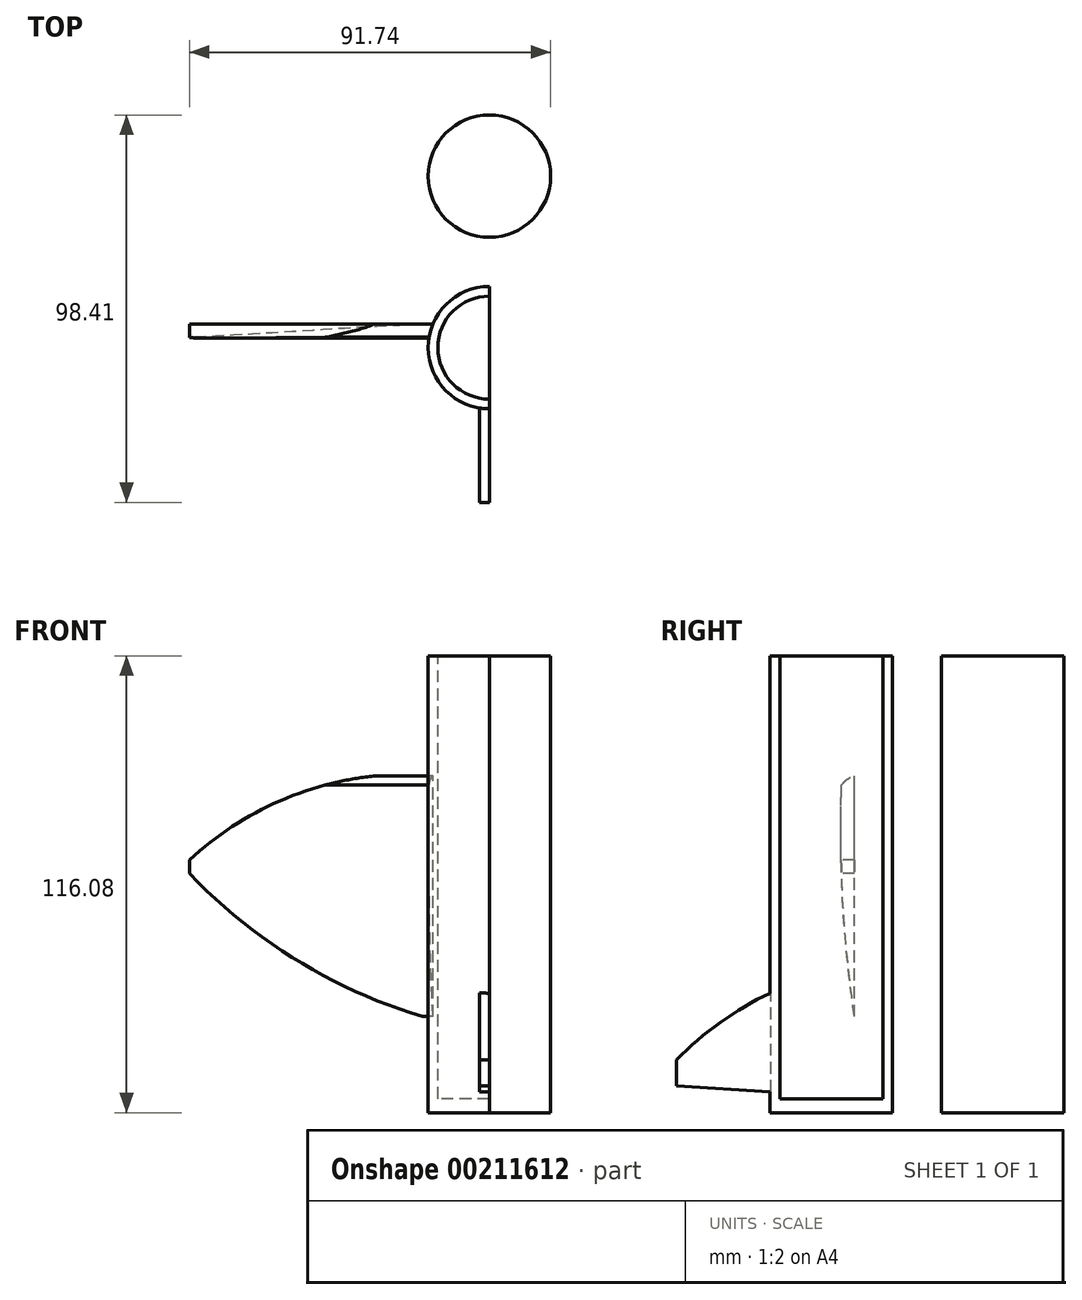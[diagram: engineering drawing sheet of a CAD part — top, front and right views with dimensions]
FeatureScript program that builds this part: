
annotation { "Feature Type Name" : "Feature", "Feature Type Description" : "" }
export const myFeature = defineFeature(function(context is Context, id is Id, definition is map)
    precondition{}
    {
        {
            var Q0;
            Q0=qCreatedBy(makeId("Front.planeOp"),FACE);
            var sketch = newSketch(context, id + "F0", { "sketchPlane" : qUnion([Q0])});
            skLineSegment(sketch, "E0", {"start": v(0, 0) * mm, "end": v(0, 31.92) * mm, "construction": true});
            skLineSegment(sketch, "E1", {"start": v(0, 31.92) * mm, "end": v(15.51, 0) * mm});
            skLineSegment(sketch, "E2", {"start": v(15.51, 0) * mm, "end": v(0, 0) * mm});
            skSolve(sketch);
        }
        {
            var Q0;
            Q0=sQuery(id+"F0.wireOp",EDGE,"E2");
            var Q1;
            Q1=sQuery(id+"F0.wireOp",EDGE,"E1");
            var Q2;
            Q2=sQuery(id+"F0.wireOp",EDGE,"E0");
            revolve(context, id + "F1", {"bodyType" : ToolBodyType.SURFACE, "surfaceEntities" : qUnion([Q0, Q1]), "axis" : qUnion([Q2]), "revolveType" : RevolveType.FULL});
        }
        {
            var Q0;
            Q0=makeQuery(id+"F1.opRevolve","SWEPT_FACE",FACE,{"disambiguationData":[OSD([sQuery(id+"F0.wireOp",EDGE,"E2")])]});
            var sketch = newSketch(context, id + "F2", { "sketchPlane" : qUnion([Q0])});
            skCircle(sketch, "E3", {"center": v(0, 0) * mm, "radius": 15.54 * mm});
            skSolve(sketch);
        }
        {
            var Q0;
            Q0 = qSketchRegion(id + "F2", true);
            extrude(context, id + "F3", {"entities" : qUnion([Q0]), "depth" : 116.08 * mm});
        }
        {
            var Q0;
            Q0=qCreatedBy(makeId("Right.planeOp"),FACE);
            var sketch = newSketch(context, id + "F4", { "sketchPlane" : qUnion([Q0])});
            skLineSegment(sketch, "E4", {"start": v(-11.39, -83.9) * mm, "end": v(-11.39, -111.03) * mm});
            skArc(sketch, "E5", {"start": v(-11.39, -83.9) * mm, "mid": v(-26.33, -91.85) * mm, "end": v(-39.3, -102.7) * mm});
            skLineSegment(sketch, "E6", {"start": v(-39.3, -102.7) * mm, "end": v(-39.3, -109.22) * mm});
            skLineSegment(sketch, "E7", {"start": v(-39.3, -109.22) * mm, "end": v(-11.39, -111.03) * mm});
            skSolve(sketch);
        }
        {
            var Q0;
            Q0 = qSketchRegion(id + "F4", true);
            extrude(context, id + "F5", {"entities" : qUnion([Q0]), "operationType" : NewBodyOperationType.ADD, "depth" : 2.54 * mm, "hasSecondDirection" : true, "secondDirectionOppositeDirection" : true, "secondDirectionDepth" : 2.54 * mm});
        }
        {
            var Q0;
            Q0=qCreatedBy(makeId("Right.planeOp"),FACE);
            var sketch = newSketch(context, id + "F6", { "sketchPlane" : qUnion([Q0])});
            skArc(sketch, "E8", {"start": v(5.92, -30.56) * mm, "mid": v(4.05, -31.4) * mm, "end": v(2.62, -32.86) * mm});
            skLineSegment(sketch, "E9", {"start": v(5.92, -30.56) * mm, "end": v(5.92, -91.67) * mm});
            skArc(sketch, "E10", {"start": v(2.62, -32.86) * mm, "mid": v(2.92, -62.34) * mm, "end": v(5.92, -91.67) * mm});
            skSolve(sketch);
        }
        {
            var Q0;
            Q0 = qSketchRegion(id + "F6", true);
            extrude(context, id + "F7", {"entities" : qUnion([Q0]), "operationType" : NewBodyOperationType.ADD, "depth" : 76.2 * mm, "hasSecondDirection" : true, "secondDirectionOppositeDirection" : true, "secondDirectionDepth" : 76.2 * mm});
        }
        {
            var Q0;
            Q0=qCreatedBy(makeId("Front.planeOp"),FACE);
            var sketch = newSketch(context, id + "F8", { "sketchPlane" : qUnion([Q0])});
            skArc(sketch, "E11", {"start": v(-15.61, -30.25) * mm, "mid": v(-51.75, -36.24) * mm, "end": v(-81.63, -57.44) * mm});
            skLineSegment(sketch, "E12", {"start": v(-81.63, -57.44) * mm, "end": v(-81.63, -24.7) * mm});
            skLineSegment(sketch, "E13", {"start": v(-81.63, -24.7) * mm, "end": v(-15.61, -30.25) * mm});
            skSolve(sketch);
        }
        {
            var Q0;
            Q0 = qSketchRegion(id + "F8", true);
            extrude(context, id + "F9", {"entities" : qUnion([Q0]), "operationType" : NewBodyOperationType.REMOVE, "oppositeDirection" : true, "depth" : 72.9 * mm});
        }
        {
            var Q0;
            Q0=qCreatedBy(makeId("Front.planeOp"),FACE);
            var sketch = newSketch(context, id + "F10", { "sketchPlane" : qUnion([Q0])});
            skArc(sketch, "E14", {"start": v(-76.62, -54.9) * mm, "mid": v(-49, -77.33) * mm, "end": v(-16.5, -91.8) * mm});
            skLineSegment(sketch, "E15", {"start": v(-76.62, -54.9) * mm, "end": v(-93.96, -110.26) * mm});
            skLineSegment(sketch, "E16", {"start": v(-93.96, -110.26) * mm, "end": v(-16.5, -91.8) * mm});
            skSolve(sketch);
        }
        {
            var Q0;
            Q0=makeQuery(id+"F10.imprint","IMPRINT",FACE,{"disambiguationData":[TD([[makeQuery(id+"F10.imprint","IMPRINT",EDGE,{"derivedFrom":sQuery(id+"F10.wireOp",EDGE,"E14")}),-1.0]])]});
            extrude(context, id + "F11", {"entities" : qUnion([Q0]), "operationType" : NewBodyOperationType.REMOVE, "oppositeDirection" : true, "depth" : 25.4 * mm});
        }
        {
            var Q0;
            Q0=qCreatedBy(makeId("Top.planeOp"),FACE);
            var sketch = newSketch(context, id + "F12", { "sketchPlane" : qUnion([Q0])});
            skCircle(sketch, "E17", {"center": v(0, 0) * mm, "radius": 13.08 * mm});
            skSolve(sketch);
        }
        {
            var Q0;
            Q0 = qSketchRegion(id + "F12", true);
            extrude(context, id + "F13", {"entities" : qUnion([Q0]), "operationType" : NewBodyOperationType.REMOVE, "oppositeDirection" : true, "depth" : 112.52 * mm});
        }
        {
            var Q0;
            Q0=qCreatedBy(makeId("Right.planeOp"),FACE);
            var sketch = newSketch(context, id + "F14", { "sketchPlane" : qUnion([Q0])});
            skLineSegment(sketch, "E18.bottom", {"start": v(-61.48, 42.63) * mm, "end": v(54.73, 42.63) * mm});
            skLineSegment(sketch, "E18.top", {"start": v(-61.48, -154.7) * mm, "end": v(54.73, -154.7) * mm});
            skLineSegment(sketch, "E18.left", {"start": v(-61.48, 42.63) * mm, "end": v(-61.48, -154.7) * mm});
            skLineSegment(sketch, "E18.right", {"start": v(54.73, 42.63) * mm, "end": v(54.73, -154.7) * mm});
            skSolve(sketch);
        }
        {
            var Q0;
            Q0 = qSketchRegion(id + "F14", true);
            extrude(context, id + "F15", {"entities" : qUnion([Q0]), "operationType" : NewBodyOperationType.REMOVE, "depth" : 105.16 * mm});
        }
        {
            var Q0;
            Q0=qCreatedBy(makeId("Top.planeOp"),FACE);
            var sketch = newSketch(context, id + "F16", { "sketchPlane" : qUnion([Q0])});
            skCircle(sketch, "E19", {"center": v(0, 43.56) * mm, "radius": 15.54 * mm});
            skSolve(sketch);
        }
        {
            var Q0;
            Q0 = qSketchRegion(id + "F16", true);
            extrude(context, id + "F17", {"entities" : qUnion([Q0]), "oppositeDirection" : true, "depth" : 116.08 * mm});
        }
    });
